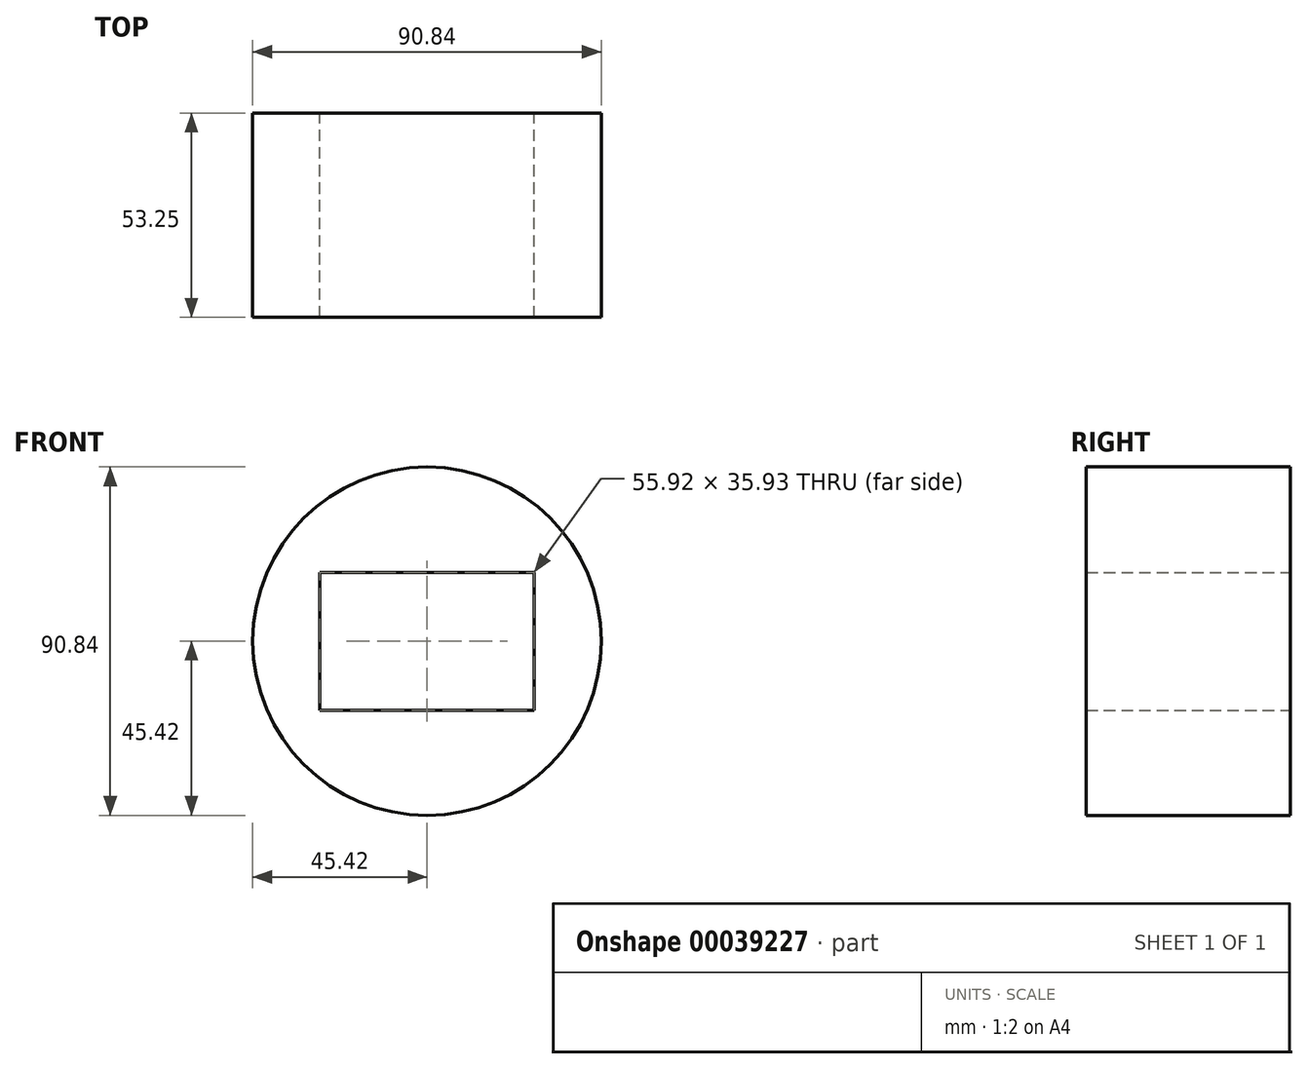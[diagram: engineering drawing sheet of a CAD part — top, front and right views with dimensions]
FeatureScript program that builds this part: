
annotation { "Feature Type Name" : "Feature", "Feature Type Description" : "" }
export const myFeature = defineFeature(function(context is Context, id is Id, definition is map)
    precondition{}
    {
        {
            var Q0;
            Q0=qCreatedBy(makeId("Front.planeOp"),FACE);
            var sketch = newSketch(context, id + "F0", { "sketchPlane" : qUnion([Q0])});
            skCircle(sketch, "E0", {"center": v(0, 0) * mm, "radius": 45.42 * mm});
            skLineSegment(sketch, "E1.rect.bottom", {"start": v(27.96, -17.97) * mm, "end": v(-27.96, -17.97) * mm});
            skLineSegment(sketch, "E1.rect.top", {"start": v(27.96, 17.97) * mm, "end": v(-27.96, 17.97) * mm});
            skLineSegment(sketch, "E1.rect.left", {"start": v(27.96, -17.97) * mm, "end": v(27.96, 17.97) * mm});
            skLineSegment(sketch, "E1.rect.right", {"start": v(-27.96, -17.97) * mm, "end": v(-27.96, 17.97) * mm});
            skSolve(sketch);
        }
        {
            var Q0;
            Q0=makeQuery(id+"F0.imprint","IMPRINT",FACE,{"disambiguationData":[TD([[makeQuery(id+"F0.imprint","IMPRINT",EDGE,{"derivedFrom":sQuery(id+"F0.wireOp",EDGE,"E0")}),1.0]])]});
            extrude(context, id + "F1", {"entities" : qUnion([Q0]), "depth" : 53.25 * mm});
        }
    });
